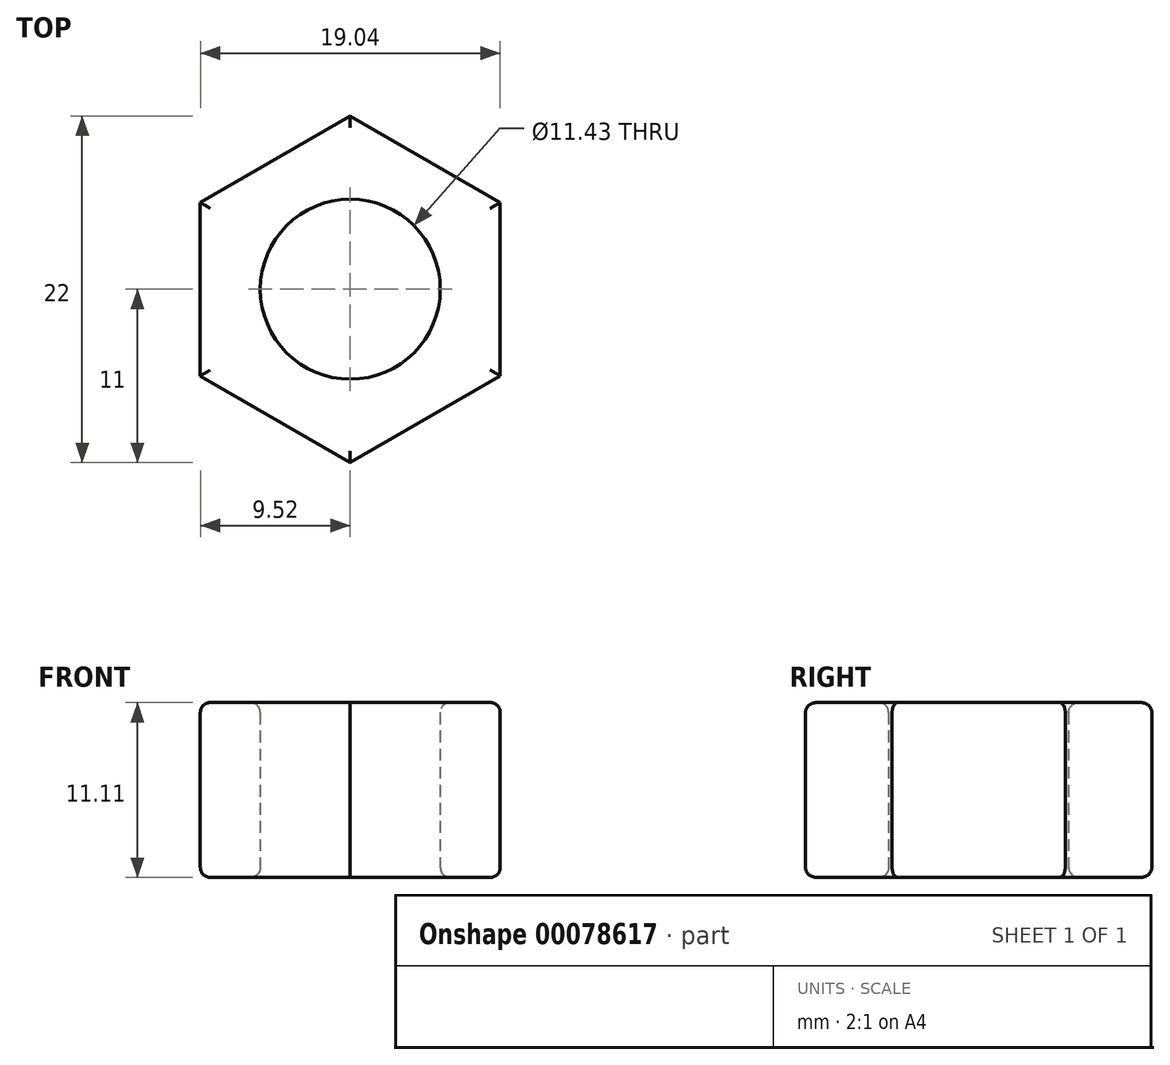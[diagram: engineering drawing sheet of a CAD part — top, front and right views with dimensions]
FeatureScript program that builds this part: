
annotation { "Feature Type Name" : "Feature", "Feature Type Description" : "" }
export const myFeature = defineFeature(function(context is Context, id is Id, definition is map)
    precondition{}
    {
        {
            var Q0;
            Q0=qCreatedBy(makeId("Top.planeOp"),FACE);
            var sketch = newSketch(context, id + "F0", { "sketchPlane" : qUnion([Q0])});
            skCircle(sketch, "E0", {"center": v(0, 0) * mm, "radius": 5.72 * mm});
            skLineSegment(sketch, "E1", {"start": v(0, 0) * mm, "end": v(0, 14.03) * mm, "construction": true});
            skLineSegment(sketch, "E2", {"start": v(0, 0) * mm, "end": v(12.98, 0) * mm, "construction": true});
            skCircle(sketch, "E3.cCircle", {"center": v(0, 0) * mm, "radius": 11 * mm, "construction": true});
            skLineSegment(sketch, "E3.0", {"start": v(9.52, 5.5) * mm, "end": v(9.52, -5.5) * mm});
            skLineSegment(sketch, "E3.1", {"start": v(9.52, -5.5) * mm, "end": v(0, -11) * mm});
            skLineSegment(sketch, "E3.2", {"start": v(0, -11) * mm, "end": v(-9.52, -5.5) * mm});
            skLineSegment(sketch, "E3.3", {"start": v(-9.52, -5.5) * mm, "end": v(-9.52, 5.5) * mm});
            skLineSegment(sketch, "E3.4", {"start": v(-9.52, 5.5) * mm, "end": v(0, 11) * mm});
            skLineSegment(sketch, "E3.5", {"start": v(0, 11) * mm, "end": v(9.52, 5.5) * mm});
            skSolve(sketch);
        }
        {
            var Q0;
            Q0 = qSketchRegion(id + "F0", true);
            extrude(context, id + "F1", {"entities" : qUnion([Q0]), "depth" : 11.1 * mm});
        }
        {
            var Q0;
            Q0=makeQuery(id+"F1.opExtrude","CAP_EDGE",EDGE,{"disambiguationData":[OSD([sQuery(id+"F0.wireOp",EDGE,"E0")])],"isStart":false});
            var Q1;
            Q1=makeQuery(id+"F1.opExtrude","CAP_EDGE",EDGE,{"disambiguationData":[OSD([sQuery(id+"F0.wireOp",EDGE,"E0")])],"isStart":true});
            var Q2;
            Q2=makeQuery(id+"F1.opExtrude","CAP_EDGE",EDGE,{"disambiguationData":[OSD([sQuery(id+"F0.wireOp",EDGE,"E3.4")])],"isStart":false});
            var Q3;
            Q3=makeQuery(id+"F1.opExtrude","CAP_EDGE",EDGE,{"disambiguationData":[OSD([sQuery(id+"F0.wireOp",EDGE,"E3.5")])],"isStart":false});
            var Q4;
            Q4=makeQuery(id+"F1.opExtrude","CAP_EDGE",EDGE,{"disambiguationData":[OSD([sQuery(id+"F0.wireOp",EDGE,"E3.3")])],"isStart":false});
            var Q5;
            Q5=makeQuery(id+"F1.opExtrude","CAP_EDGE",EDGE,{"disambiguationData":[OSD([sQuery(id+"F0.wireOp",EDGE,"E3.2")])],"isStart":false});
            var Q6;
            Q6=makeQuery(id+"F1.opExtrude","CAP_EDGE",EDGE,{"disambiguationData":[OSD([sQuery(id+"F0.wireOp",EDGE,"E3.1")])],"isStart":false});
            var Q7;
            Q7=makeQuery(id+"F1.opExtrude","CAP_EDGE",EDGE,{"disambiguationData":[OSD([sQuery(id+"F0.wireOp",EDGE,"E3.0")])],"isStart":false});
            var Q8;
            Q8=makeQuery(id+"F1.opExtrude","CAP_EDGE",EDGE,{"disambiguationData":[OSD([sQuery(id+"F0.wireOp",EDGE,"E3.5")])],"isStart":true});
            var Q9;
            Q9=makeQuery(id+"F1.opExtrude","CAP_EDGE",EDGE,{"disambiguationData":[OSD([sQuery(id+"F0.wireOp",EDGE,"E3.4")])],"isStart":true});
            var Q10;
            Q10=makeQuery(id+"F1.opExtrude","CAP_EDGE",EDGE,{"disambiguationData":[OSD([sQuery(id+"F0.wireOp",EDGE,"E3.3")])],"isStart":true});
            var Q11;
            Q11=makeQuery(id+"F1.opExtrude","CAP_EDGE",EDGE,{"disambiguationData":[OSD([sQuery(id+"F0.wireOp",EDGE,"E3.1")])],"isStart":true});
            var Q12;
            Q12=makeQuery(id+"F1.opExtrude","CAP_EDGE",EDGE,{"disambiguationData":[OSD([sQuery(id+"F0.wireOp",EDGE,"E3.2")])],"isStart":true});
            var Q13;
            Q13=makeQuery(id+"F1.opExtrude","CAP_EDGE",EDGE,{"disambiguationData":[OSD([sQuery(id+"F0.wireOp",EDGE,"E3.0")])],"isStart":true});
            fillet(context, id + "F2", {"entities" : qUnion([Q0, Q1, Q2, Q3, Q4, Q5, Q6, Q7, Q8, Q9, Q10, Q11, Q12, Q13]), "radius" : 0.64 * mm, "tangentPropagation" : true, "allowEdgeOverflow" : false});
        }
    });
